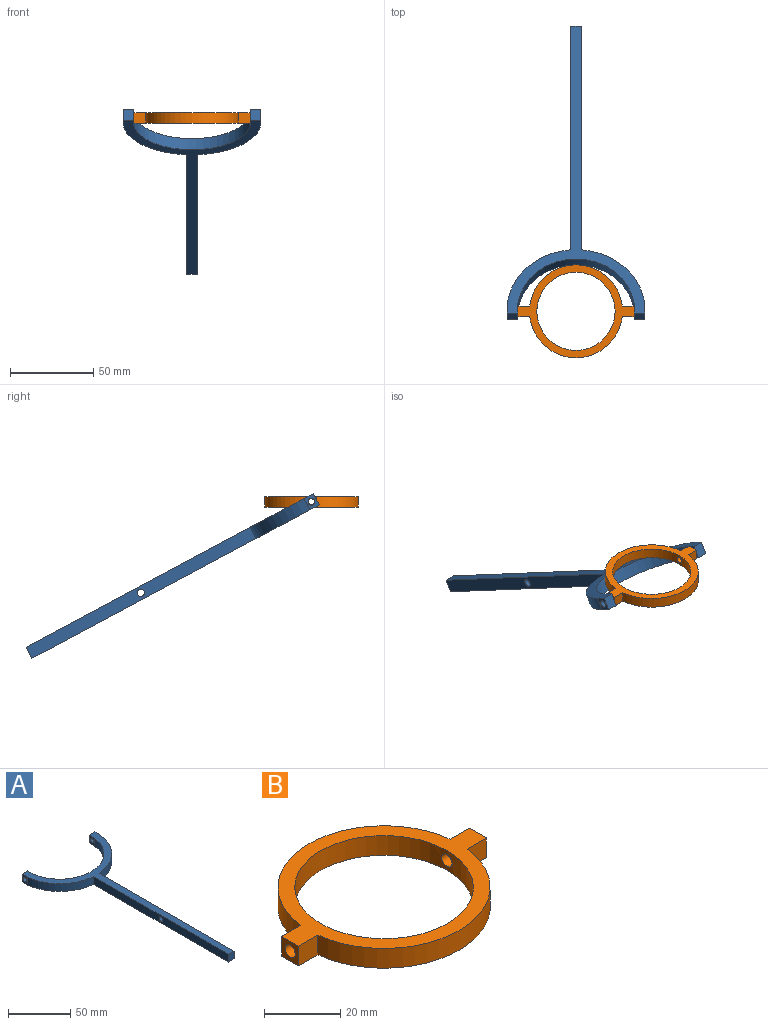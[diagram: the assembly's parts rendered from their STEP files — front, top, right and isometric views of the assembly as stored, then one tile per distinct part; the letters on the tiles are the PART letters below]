
ASSEMBLY  parts=2 mates=1
PART A: 17 faces, bbox 82.6x195.6x7.6 mm
  f0: cylinder r=35.25mm len=69.85mm, axis (0,0,-1), area 770.9mm2, adj f6,f7,f10,f12
  f1: cylinder r=41.54mm len=38.1mm, axis (0,0,-1), area 437mm2, adj f2,f6,f7,f9
  f2: plane 152.52x7.62mm, normal (-1,0,0), area 1147.1mm2, adj f1,f3,f6,f7,f8
  f3: plane 7.62x6.35mm, normal (0,-1,0), area 48.4mm2, adj f2,f4,f6,f7
  f4: plane 152.52x7.62mm, normal (1,0,0), area 1147.1mm2, adj f3,f5,f6,f7,f8
  f5: cylinder r=41.54mm len=38.1mm, axis (0,0,-1), area 437mm2, adj f4,f6,f7,f13
  f6: plane 195.58x82.55mm, normal (0,0,1), area 1752.3mm2, adj f0,f1,f2,f3,f4,f5,f9,f10
  f7: plane 195.58x82.55mm, normal (0,0,-1), area 1752.3mm2, adj f0,f1,f2,f3,f4,f5,f9,f10
  f8: cylinder r=2.2mm len=6.35mm, axis (1,0,0), area 87.6mm2, adj f2,f4
  f9: plane 7.62x6.35mm, normal (-1,0,0), area 35.2mm2, adj f1,f6,f7,f11,f16
  f10: plane 7.62x6.35mm, normal (1,0,0), area 35.2mm2, adj f0,f6,f7,f11,f16
  f11: plane 7.62x6.35mm, normal (0,1,0), area 48.4mm2, adj f6,f7,f9,f10
  f12: plane 7.62x6.35mm, normal (-1,0,0), area 35.2mm2, adj f0,f6,f7,f14,f15
  f13: plane 7.62x6.35mm, normal (1,0,0), area 35.2mm2, adj f5,f6,f7,f14,f15
  f14: plane 7.62x6.35mm, normal (0,1,0), area 48.4mm2, adj f6,f7,f12,f13
  f15: cylinder r=2.05mm len=6.35mm, axis (1,0,0), area 81.7mm2, adj f12,f13
  f16: cylinder r=2.05mm len=6.35mm, axis (1,0,0), area 81.7mm2, adj f9,f10
PART B: 13 faces, bbox 69.9x55.9x6.4 mm
  f0: plane 7.17x6.35mm, normal (0,-1,0), area 45.5mm2, adj f1,f8,f9,f10
  f1: cylinder r=27.94mm len=55.52mm, axis (0,0,-1), area 517mm2, adj f0,f2,f9,f10
  f2: plane 7.17x6.35mm, normal (0,-1,0), area 45.5mm2, adj f1,f3,f9,f10
  f3: plane 6.35x6.35mm, normal (1,0,0), area 28.9mm2, adj f2,f4,f9,f10,f12
  f4: plane 7.17x6.35mm, normal (0,1,0), area 45.5mm2, adj f3,f5,f9,f10
  f5: cylinder r=27.94mm len=55.52mm, axis (0,0,-1), area 517mm2, adj f4,f6,f9,f10
  f6: plane 7.17x6.35mm, normal (0,1,0), area 45.5mm2, adj f5,f8,f9,f10
  f7: cylinder r=23.49mm len=46.99mm, axis (0,0,-1), area 914.5mm2, adj f9,f10,f11,f12
  f8: plane 6.35x6.35mm, normal (-1,0,0), area 28.9mm2, adj f0,f6,f9,f10,f11
  f9: plane 69.85x55.88mm, normal (0,0,1), area 807.7mm2, adj f0,f1,f2,f3,f4,f5,f6,f7
  f10: plane 69.85x55.88mm, normal (0,0,-1), area 807.7mm2, adj f0,f1,f2,f3,f4,f5,f6,f7
  f11: cylinder r=1.91mm len=11.51mm, axis (1,0,0), area 137.7mm2, adj f7,f8
  f12: cylinder r=1.91mm len=11.51mm, axis (1,0,0), area 137.7mm2, adj f3,f7
PLACE A rot(axis=(1,0,0),151.9deg) t=(-1.88,-181.12,170.38)mm
PLACE B t=(-1.88,-185.71,165.34)mm
MATE revolute B.f11 <-> A.f15  axis (1,0,0) through (33.05,-185.71,168.51)mm
